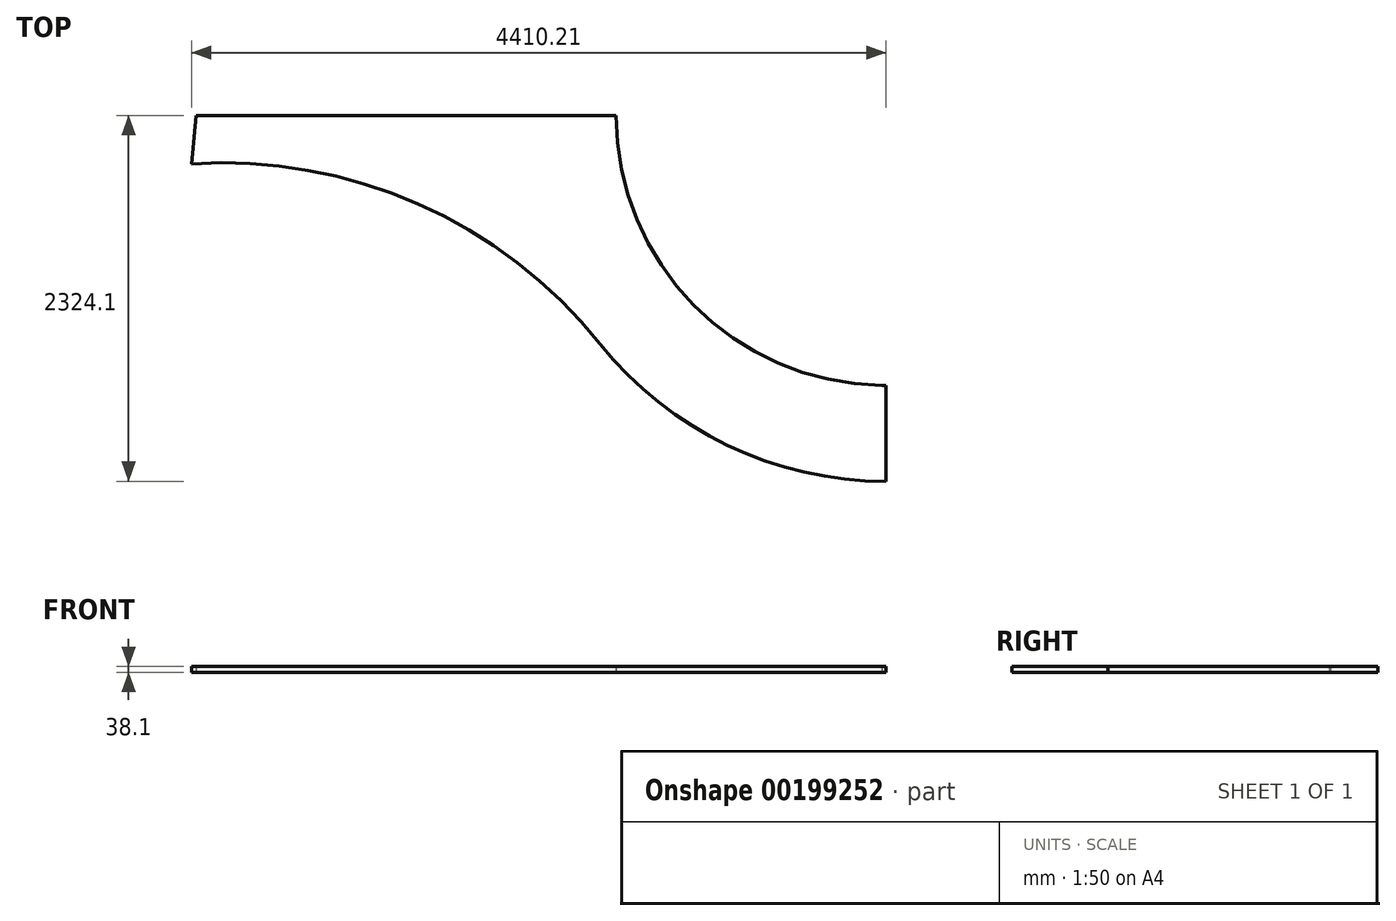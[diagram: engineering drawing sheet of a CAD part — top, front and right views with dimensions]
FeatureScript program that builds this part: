
annotation { "Feature Type Name" : "Feature", "Feature Type Description" : "" }
export const myFeature = defineFeature(function(context is Context, id is Id, definition is map)
    precondition{}
    {
        {
            var Q0;
            Q0=qCreatedBy(makeId("Top.planeOp"),FACE);
            var sketch = newSketch(context, id + "F0", { "sketchPlane" : qUnion([Q0])});
            skLineSegment(sketch, "E0", {"start": v(-2316.67, 127.82) * mm, "end": v(349.93, 127.82) * mm});
            skLineSegment(sketch, "E1", {"start": v(2064.43, -1586.68) * mm, "end": v(2064.43, -2196.28) * mm});
            skArc(sketch, "E2", {"start": v(2064.43, -1586.68) * mm, "mid": v(852.1, -1084.52) * mm, "end": v(349.93, 127.82) * mm});
            skArc(sketch, "E3.0", {"start": v(2064.43, -1891.48) * mm, "mid": v(1189.8, -1692.24) * mm, "end": v(487.77, -1133.82) * mm});
            skArc(sketch, "E4.0", {"start": v(2064.43, -2196.28) * mm, "mid": v(1057.78, -1966.96) * mm, "end": v(249.79, -1324.25) * mm});
            skLineSegment(sketch, "E5", {"start": v(-2316.67, 127.82) * mm, "end": v(-2345.78, -179.16) * mm});
            skPoint(sketch, "E6", {"position": v(-2316.67, 127.82) * mm});
            skArc(sketch, "E7", {"start": v(487.77, -1133.82) * mm, "mid": v(-608.98, -238.62) * mm, "end": v(-1976.45, 127.82) * mm});
            skArc(sketch, "E8.0", {"start": v(249.79, -1324.25) * mm, "mid": v(-907.75, -433.81) * mm, "end": v(-2345.78, -179.16) * mm});
            skPoint(sketch, "E9.orphan", {"position": v(-2436.3, -1133.82) * mm});
            skLineSegment(sketch, "E10.0", {"start": v(-2291.3, 126.27) * mm, "end": v(-2317.7, -152.02) * mm});
            skArc(sketch, "E11.0", {"start": v(300.99, -1348.25) * mm, "mid": v(-872.47, -421.75) * mm, "end": v(-2343.36, -153.55) * mm});
            skArc(sketch, "E12.0", {"start": v(2064.43, -2170.88) * mm, "mid": v(1097.91, -1957.81) * mm, "end": v(310.57, -1358.11) * mm});
            skLineSegment(sketch, "E13.0", {"start": v(2039.03, -1586.5) * mm, "end": v(2039.03, -2170.74) * mm});
            skLineSegment(sketch, "E14", {"start": v(-2343.36, -153.55) * mm, "end": v(-2316.67, 127.82) * mm});
            skLineSegment(sketch, "E15", {"start": v(-2343.36, -153.55) * mm, "end": v(-2317.7, -152.02) * mm});
            skLineSegment(sketch, "E16", {"start": v(-2291.3, 126.27) * mm, "end": v(-2316.67, 127.82) * mm});
            skLineSegment(sketch, "E17.bottom", {"start": v(2039.03, -1586.5) * mm, "end": v(2064.43, -1586.5) * mm});
            skLineSegment(sketch, "E17.top", {"start": v(2039.03, -1586.68) * mm, "end": v(2064.43, -1586.68) * mm});
            skLineSegment(sketch, "E17.left", {"start": v(2039.03, -1586.5) * mm, "end": v(2039.03, -1586.68) * mm});
            skLineSegment(sketch, "E17.right", {"start": v(2064.43, -1586.5) * mm, "end": v(2064.43, -1586.68) * mm});
            skLineSegment(sketch, "E18", {"start": v(2064.43, -2170.88) * mm, "end": v(2039.03, -2170.74) * mm});
            skLineSegment(sketch, "E19", {"start": v(300.99, -1348.25) * mm, "end": v(310.57, -1358.11) * mm});
            skSolve(sketch);
        }
        {
            var Q0;
            Q0=qSketchRegion(id+"F0",true);
            extrude(context, id + "F1", {"entities" : qUnion([Q0]), "endBound" : BoundingType.SYMMETRIC, "depth" : 38.1 * mm});
        }
    });
